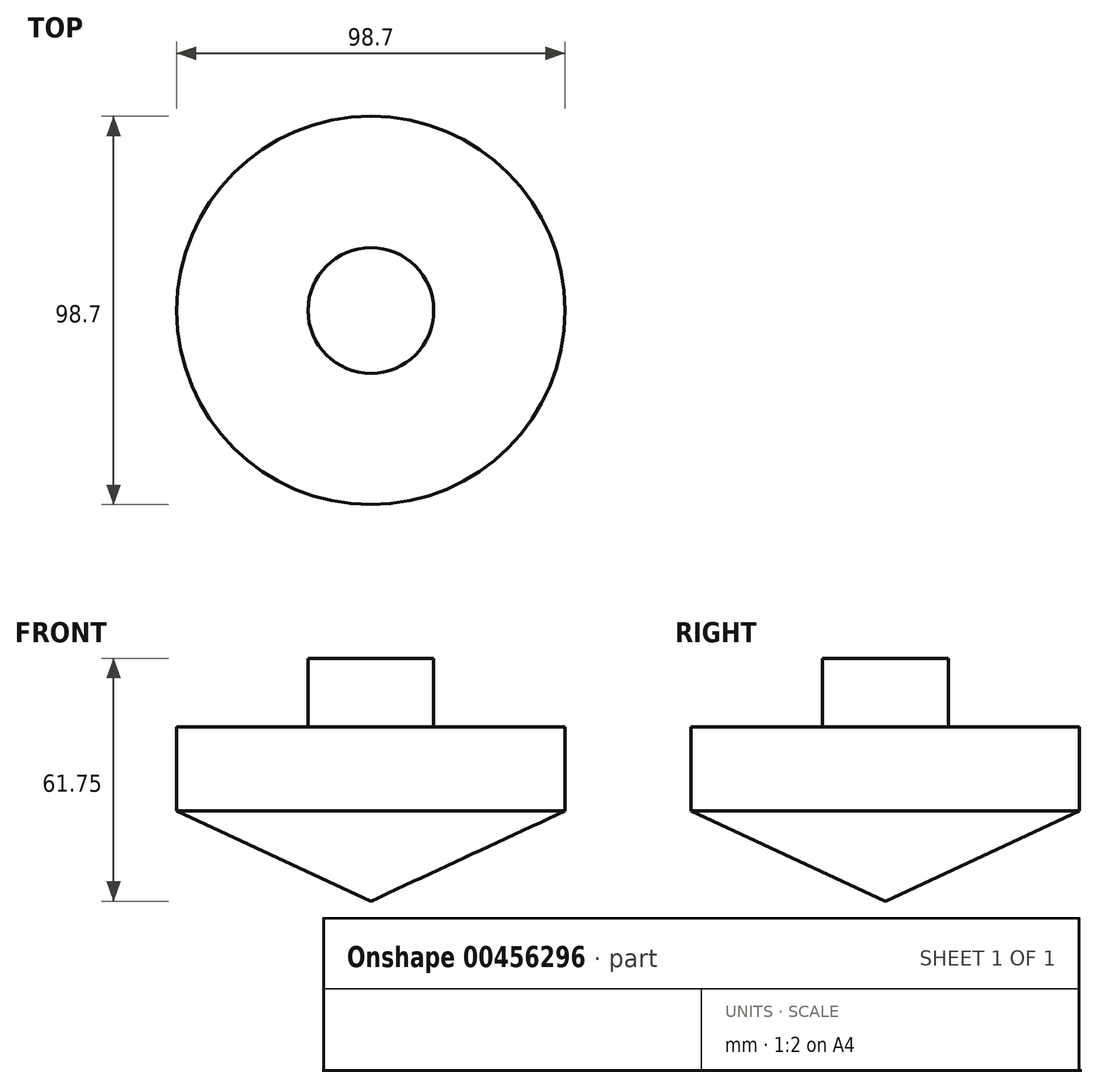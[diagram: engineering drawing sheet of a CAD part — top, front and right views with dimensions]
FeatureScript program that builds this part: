
annotation { "Feature Type Name" : "Feature", "Feature Type Description" : "" }
export const myFeature = defineFeature(function(context is Context, id is Id, definition is map)
    precondition{}
    {
        {
            var Q0;
            Q0=qCreatedBy(makeId("Front.planeOp"),FACE);
            var sketch = newSketch(context, id + "F0", { "sketchPlane" : qUnion([Q0])});
            skLineSegment(sketch, "E0", {"start": v(0, 0) * mm, "end": v(49.35, 22.96) * mm});
            skLineSegment(sketch, "E1", {"start": v(49.35, 22.96) * mm, "end": v(49.35, 44.35) * mm});
            skLineSegment(sketch, "E2", {"start": v(49.35, 44.35) * mm, "end": v(15.97, 44.35) * mm});
            skLineSegment(sketch, "E3", {"start": v(15.97, 44.35) * mm, "end": v(15.97, 61.75) * mm});
            skLineSegment(sketch, "E4", {"start": v(15.97, 61.75) * mm, "end": v(0, 61.75) * mm});
            skLineSegment(sketch, "E5", {"start": v(0, 61.75) * mm, "end": v(0, 0) * mm});
            skSolve(sketch);
        }
        {
            var Q0;
            Q0 = qSketchRegion(id + "F0", true);
            var Q1;
            Q1=sQuery(id+"F0.wireOp",EDGE,"E5");
            revolve(context, id + "F1", {"entities" : qUnion([Q0]), "axis" : qUnion([Q1]), "revolveType" : RevolveType.FULL});
        }
    });
